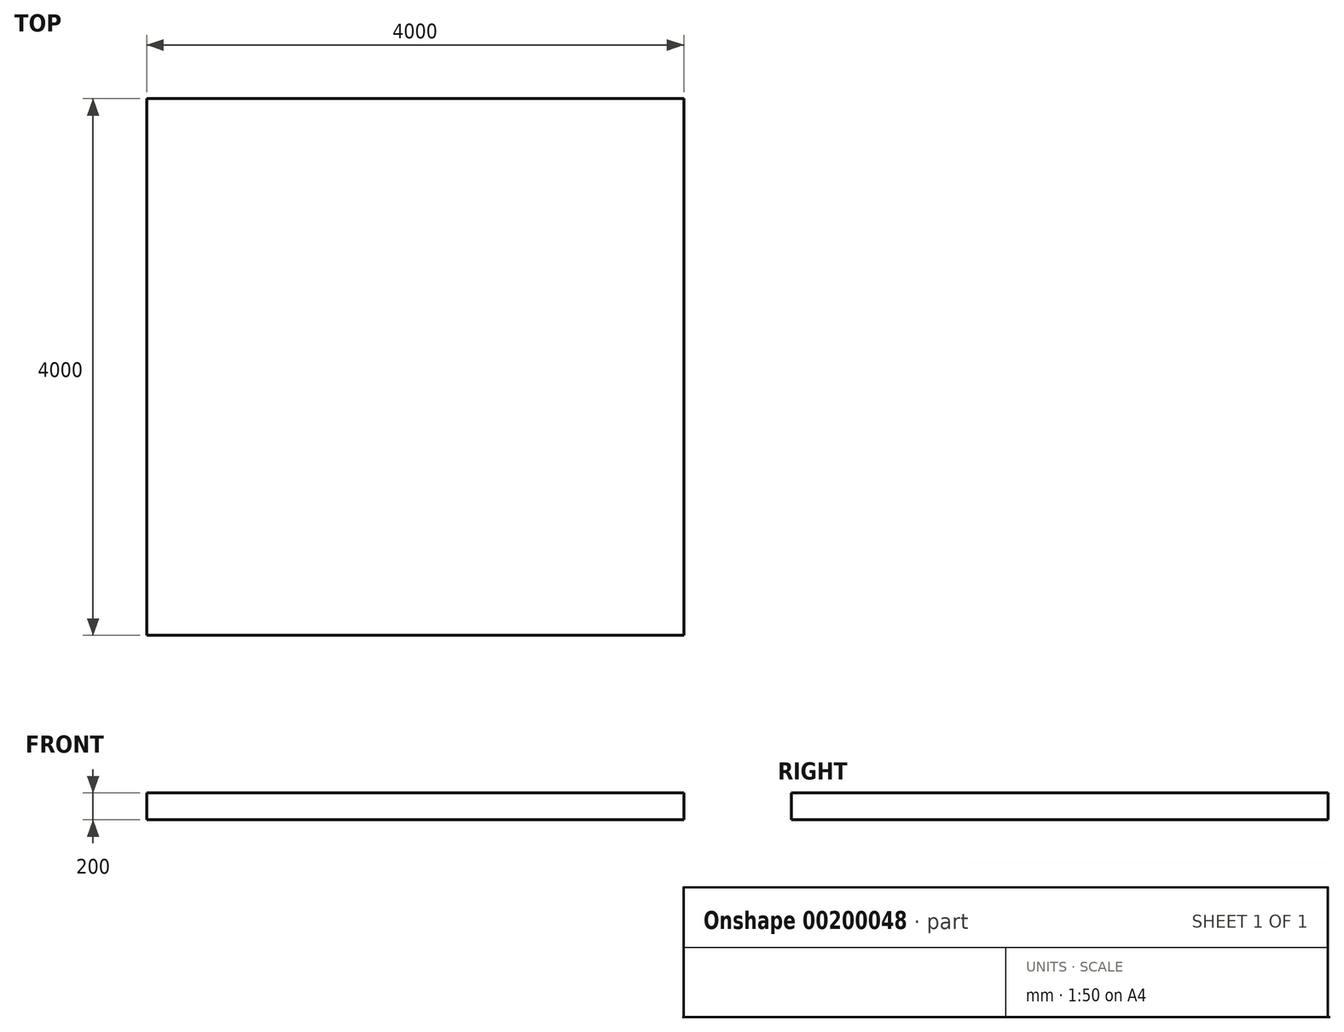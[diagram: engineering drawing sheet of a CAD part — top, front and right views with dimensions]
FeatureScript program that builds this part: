
annotation { "Feature Type Name" : "Feature", "Feature Type Description" : "" }
export const myFeature = defineFeature(function(context is Context, id is Id, definition is map)
    precondition{}
    {
        {
            var Q0;
            Q0=qCreatedBy(makeId("Top.planeOp"),FACE);
            var sketch = newSketch(context, id + "F0", { "sketchPlane" : qUnion([Q0])});
            skLineSegment(sketch, "E0.bottom", {"start": v(-2000, 2000) * mm, "end": v(2000, 2000) * mm});
            skLineSegment(sketch, "E0.top", {"start": v(-2000, -2000) * mm, "end": v(2000, -2000) * mm});
            skLineSegment(sketch, "E0.left", {"start": v(-2000, 2000) * mm, "end": v(-2000, -2000) * mm});
            skLineSegment(sketch, "E0.right", {"start": v(2000, 2000) * mm, "end": v(2000, -2000) * mm});
            skSolve(sketch);
        }
        {
            var Q0;
            Q0 = qSketchRegion(id + "F0", true);
            extrude(context, id + "F1", {"entities" : qUnion([Q0]), "depth" : 200 * mm});
        }
    });
